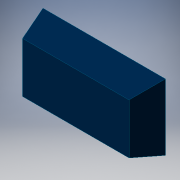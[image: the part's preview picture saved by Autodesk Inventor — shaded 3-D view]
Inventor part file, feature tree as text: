
AUTODESK INVENTOR PART (.ipt)
format: ipt  version: 2019 (Build 230136000, 136)  size: 93,696 bytes
history: native  units: in
note: dims shown in document units (in); Inventor stores cm internally (conversion verified against a paired STEP export)
features: sketch x2, plane x1, loft x1
ambient origin geometry x8: Origin, YZ Plane, XZ Plane, XY Plane, X Axis, Y Axis, Z Axis, Center Point
bodies: Solid1 (feature_tree)
feature tree (4):
  sketch  "Sketch1"  dims[d0=207.0in d1=112.0in]
  plane  "Work Plane1"
  loft  "Loft1"
  sketch  "Sketch2"  dims[d2=48.0in d3=180.0in d4=85.0in d5=0.0in d6=90.0deg d7=0.0in d8=90.0deg]
